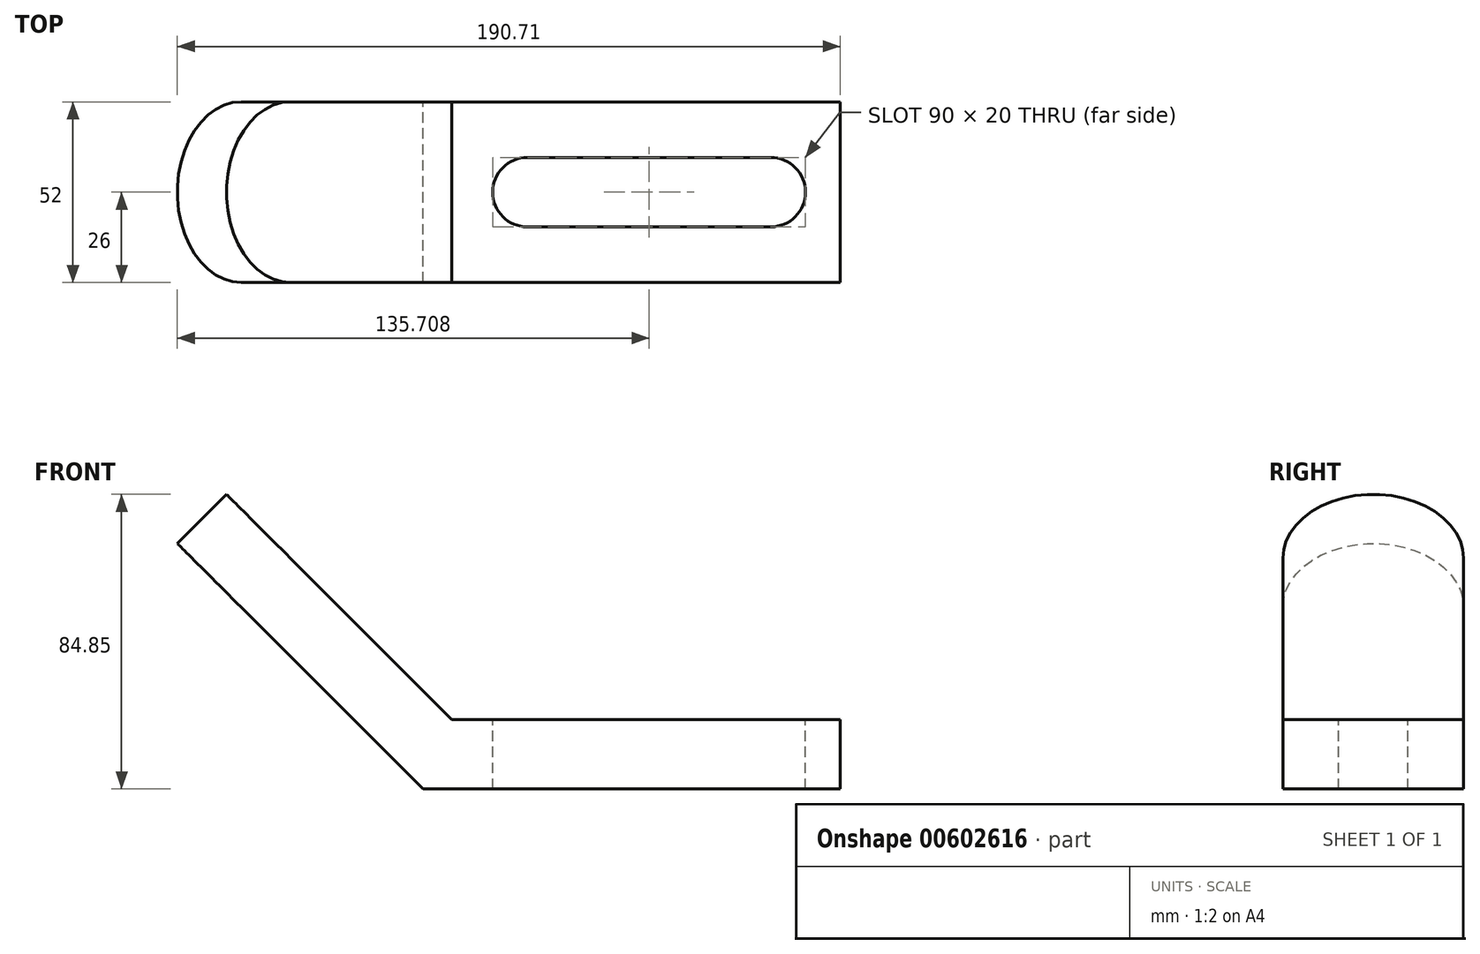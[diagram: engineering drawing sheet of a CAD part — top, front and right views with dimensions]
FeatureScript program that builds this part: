
annotation { "Feature Type Name" : "Feature", "Feature Type Description" : "" }
export const myFeature = defineFeature(function(context is Context, id is Id, definition is map)
    precondition{}
    {
        {
            var Q0;
            Q0=qCreatedBy(makeId("Front.planeOp"),FACE);
            var sketch = newSketch(context, id + "F0", { "sketchPlane" : qUnion([Q0])});
            skLineSegment(sketch, "E0.bottom", {"start": v(60.29, 8.15) * mm, "end": v(-51.43, 8.15) * mm});
            skLineSegment(sketch, "E0.top", {"start": v(60.29, -11.85) * mm, "end": v(-59.71, -11.85) * mm});
            skLineSegment(sketch, "E0.left", {"start": v(60.29, 8.15) * mm, "end": v(60.29, -11.85) * mm});
            skLineSegment(sketch, "E1.bottom", {"start": v(-59.71, -11.85) * mm, "end": v(-130.42, 58.86) * mm});
            skLineSegment(sketch, "E1.top", {"start": v(-51.43, 8.15) * mm, "end": v(-116.28, 73) * mm});
            skLineSegment(sketch, "E1.right", {"start": v(-130.42, 58.86) * mm, "end": v(-116.28, 73) * mm});
            skSolve(sketch);
        }
        {
            var Q0;
            Q0 = qSketchRegion(id + "F0", true);
            extrude(context, id + "F1", {"entities" : qUnion([Q0]), "depth" : 52 * mm, "offsetDistance" : 25 * mm});
        }
        {
            var Q0;
            Q0=makeQuery(id+"F1.opExtrude","SWEPT_FACE",FACE,{"disambiguationData":[OSD([sQuery(id+"F0.wireOp",EDGE,"E1.top")])]});
            var sketch = newSketch(context, id + "F2", { "sketchPlane" : qUnion([Q0])});
            skPoint(sketch, "E2.endSnap0", {"position": v(-133.84, -26) * mm});
            skCircle(sketch, "E3", {"center": v(-107.84, -26) * mm, "radius": 10 * mm});
            skSolve(sketch);
        }
        {
            var Q0;
            Q0 = qSketchRegion(id + "F2", true);
            extrude(context, id + "F3", {"entities" : qUnion([Q0]), "operationType" : NewBodyOperationType.REMOVE, "oppositeDirection" : true, "depth" : 20 * mm, "offsetDistance" : 25 * mm});
        }
        {
            var Q0;
            Q0=makeQuery(id+"F1.opExtrude","SWEPT_FACE",FACE,{"disambiguationData":[OSD([sQuery(id+"F0.wireOp",EDGE,"E0.bottom")])]});
            var sketch = newSketch(context, id + "F4", { "sketchPlane" : qUnion([Q0])});
            skLineSegment(sketch, "E4", {"start": v(60.29, -26) * mm, "end": v(40.29, -26) * mm});
            skPoint(sketch, "E4.endSnap0", {"position": v(60.29, -26) * mm});
            skCircle(sketch, "E5", {"center": v(40.29, -26) * mm, "radius": 10 * mm});
            skLineSegment(sketch, "E6", {"start": v(40.29, -16) * mm, "end": v(-29.71, -16) * mm});
            skLineSegment(sketch, "E7", {"start": v(-29.71, -36) * mm, "end": v(40.29, -36) * mm});
            skCircle(sketch, "E8", {"center": v(-29.71, -26) * mm, "radius": 10 * mm});
            skSolve(sketch);
        }
        {
            var Q0;
            {var subQ0=sQuery(id+"F4.wireOp",EDGE,"E6");Q0=makeQuery(id+"F4.imprint","IMPRINT",FACE,{"disambiguationData":[TD([[makeQuery(id+"F4.imprint","IMPRINT",EDGE,{"derivedFrom":subQ0}),1.0]])]});}
            var Q1;
            {var subQ0=sQuery(id+"F4.wireOp",EDGE,"E5");var subQ2=makeQuery(id+"F4.imprint","IMPRINT",VERTEX,{"derivedFrom":subQ0});Q1=makeQuery(id+"F4.imprint","IMPRINT",FACE,{"disambiguationData":[TD([[makeQuery(id+"F4.imprint","IMPRINT",EDGE,{"disambiguationData":[TD([[subQ2,-1.0]])],"derivedFrom":subQ0}),1.0]])]});}
            var Q2;
            {var subQ0=sQuery(id+"F4.wireOp",EDGE,"E8");var subQ1=makeQuery(id+"F4.imprint","INTERSECT",VERTEX,{"derivedFrom":[sQuery(id+"F4.wireOp",EDGE,"E6"),subQ0]});Q2=makeQuery(id+"F4.imprint","IMPRINT",FACE,{"disambiguationData":[TD([[makeQuery(id+"F4.imprint","IMPRINT",EDGE,{"disambiguationData":[TD([[subQ1,-1.0]])],"derivedFrom":subQ0}),1.0]])]});}
            extrude(context, id + "F5", {"entities" : qUnion([Q0, Q1, Q2]), "operationType" : NewBodyOperationType.REMOVE, "oppositeDirection" : true, "depth" : 20 * mm, "offsetDistance" : 25 * mm});
        }
        {
            var Q0;
            Q0=makeQuery(id+"F1.opExtrude","CAP_EDGE",EDGE,{"disambiguationData":[OSD([sQuery(id+"F0.wireOp",EDGE,"E1.right")])],"isStart":false});
            var Q1;
            Q1=makeQuery(id+"F1.opExtrude","CAP_EDGE",EDGE,{"disambiguationData":[OSD([sQuery(id+"F0.wireOp",EDGE,"E1.right")])],"isStart":true});
            fillet(context, id + "F6", {"entities" : qUnion([Q0, Q1]), "radius" : 26 * mm, "tangentPropagation" : true, "allowEdgeOverflow" : false});
        }
    });
